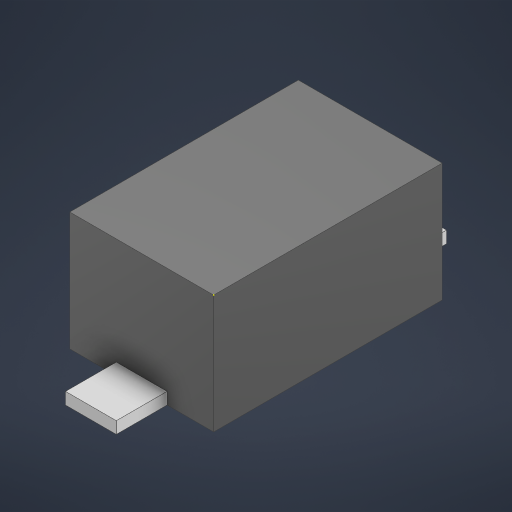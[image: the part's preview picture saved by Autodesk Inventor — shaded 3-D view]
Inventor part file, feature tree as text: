
AUTODESK INVENTOR PART (.ipt)
format: ipt  version: 2024.2 (Build 282272000, 272)  size: 182,784 bytes
history: native  units: mm
features: sketch x4, extrude x3, other x1
ambient origin geometry x8: Origin, YZ Plane, XZ Plane, XY Plane, X Axis, Y Axis, Z Axis, Center Point
bodies: Solid1 (feature_tree)
feature tree (8):
  extrude  "Extrusion1"  Depth=2.7mm
  extrude  "Extrusion2"  Depth=0.6mm
  extrude  "Extrusion3"  Depth=0.55mm
  sketch  "Sketch4"  dims[d7=0.6mm d8=0.0mm d9=0.6mm d10=0.14mm d11=0.55mm d12=1.4mm d13=0.6mm d14=0.0mm]
  sketch  "Sketch1"  dims[d0=1.7mm d1=2.7mm]
  sketch  "Sketch2"  dims[d2=1.4mm d3=0.0mm d4=0.6mm]
  sketch  "Sketch3"  dims[d5=0.14mm d6=0.55mm]
  other  "Finish1"
